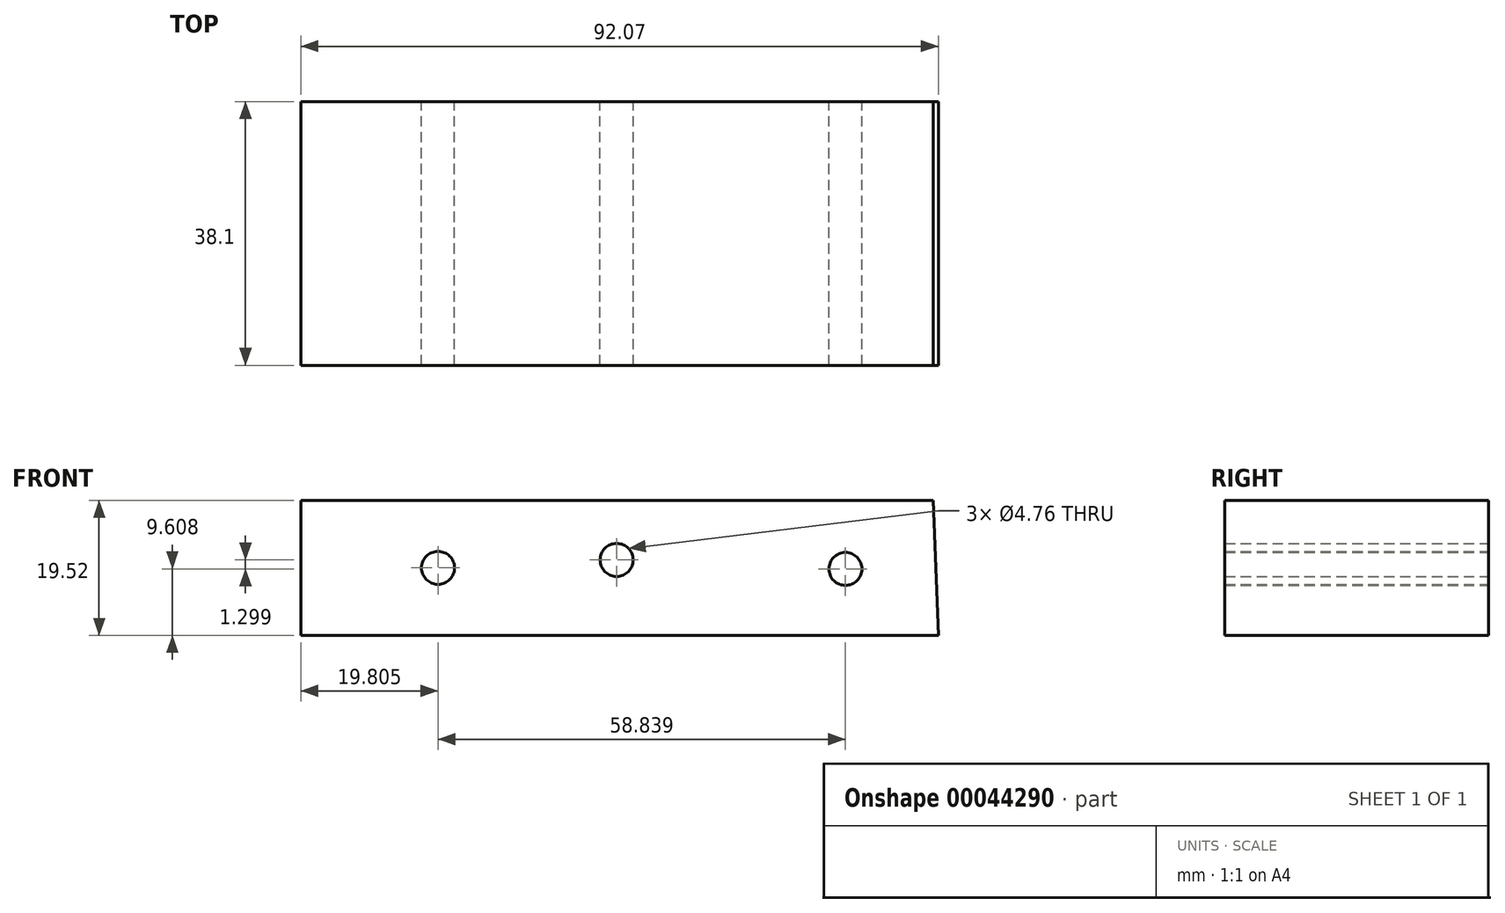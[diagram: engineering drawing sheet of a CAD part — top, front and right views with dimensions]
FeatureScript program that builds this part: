
annotation { "Feature Type Name" : "Feature", "Feature Type Description" : "" }
export const myFeature = defineFeature(function(context is Context, id is Id, definition is map)
    precondition{}
    {
        {
            var Q0;
            Q0=qCreatedBy(makeId("Front.planeOp"),FACE);
            var sketch = newSketch(context, id + "F0", { "sketchPlane" : qUnion([Q0])});
            skLineSegment(sketch, "E0", {"start": v(46.47, 0) * mm, "end": v(46.47, 0) * mm});
            skLineSegment(sketch, "E1", {"start": v(46.47, 0) * mm, "end": v(-45.6, 0) * mm});
            skLineSegment(sketch, "E2", {"start": v(-45.6, 0) * mm, "end": v(-45.6, 19.52) * mm});
            skLineSegment(sketch, "E3", {"start": v(-45.6, 19.52) * mm, "end": v(45.72, 19.52) * mm});
            skLineSegment(sketch, "E4", {"start": v(46.47, 0) * mm, "end": v(45.72, 19.52) * mm});
            skCircle(sketch, "E5", {"center": v(33.04, 9.6) * mm, "radius": 2.38 * mm});
            skCircle(sketch, "E6", {"center": v(-25.8, 9.76) * mm, "radius": 2.38 * mm});
            skPoint(sketch, "E6.centerSnap0", {"position": v(-45.6, 9.76) * mm});
            skCircle(sketch, "E7", {"center": v(0, 10.9) * mm, "radius": 2.38 * mm});
            skCircle(sketch, "E8", {"center": v(33.04, 8.8) * mm, "radius": 0.8 * mm});
            skCircle(sketch, "E9", {"center": v(32.85, 10.45) * mm, "radius": 0.86 * mm});
            skCircle(sketch, "E10", {"center": v(0.7, 10.9) * mm, "radius": 0.64 * mm});
            skCircle(sketch, "E11", {"center": v(-0.84, 10.98) * mm, "radius": 0.56 * mm});
            skCircle(sketch, "E12", {"center": v(-25.8, 9.18) * mm, "radius": 0.58 * mm});
            skCircle(sketch, "E13", {"center": v(-26.25, 10.82) * mm, "radius": 0.58 * mm});
            skSolve(sketch);
        }
        {
            var Q0;
            Q0=makeQuery(id+"F0.imprint","IMPRINT",FACE,{"disambiguationData":[TD([[makeQuery(id+"F0.imprint","IMPRINT",EDGE,{"derivedFrom":sQuery(id+"F0.wireOp",EDGE,"E0")}),1.0]])]});
            var Q1;
            Q1=makeQuery(id+"F0.imprint","IMPRINT",FACE,{"disambiguationData":[TD([[makeQuery(id+"F0.imprint","IMPRINT",EDGE,{"derivedFrom":sQuery(id+"F0.wireOp",EDGE,"E1")}),-1.0]])]});
            extrude(context, id + "F1", {"entities" : qUnion([Q0, Q1]), "endBound" : BoundingType.SYMMETRIC, "depth" : 25.4 * mm});
        }
        {
            var Q0;
            Q0 = qSketchRegion(id + "F0", true);
            extrude(context, id + "F2", {"entities" : qUnion([Q0]), "operationType" : NewBodyOperationType.ADD, "depth" : 25.4 * mm});
        }
        {
            var Q0;
            Q0 = qSketchRegion(id + "F0", true);
            extrude(context, id + "F3", {"entities" : qUnion([Q0]), "operationType" : NewBodyOperationType.ADD, "depth" : 25.4 * mm});
        }
        {
            var Q0;
            Q0 = qSketchRegion(id + "F0", true);
            extrude(context, id + "F4", {"entities" : qUnion([Q0]), "operationType" : NewBodyOperationType.ADD, "depth" : 25.4 * mm});
        }
    });
